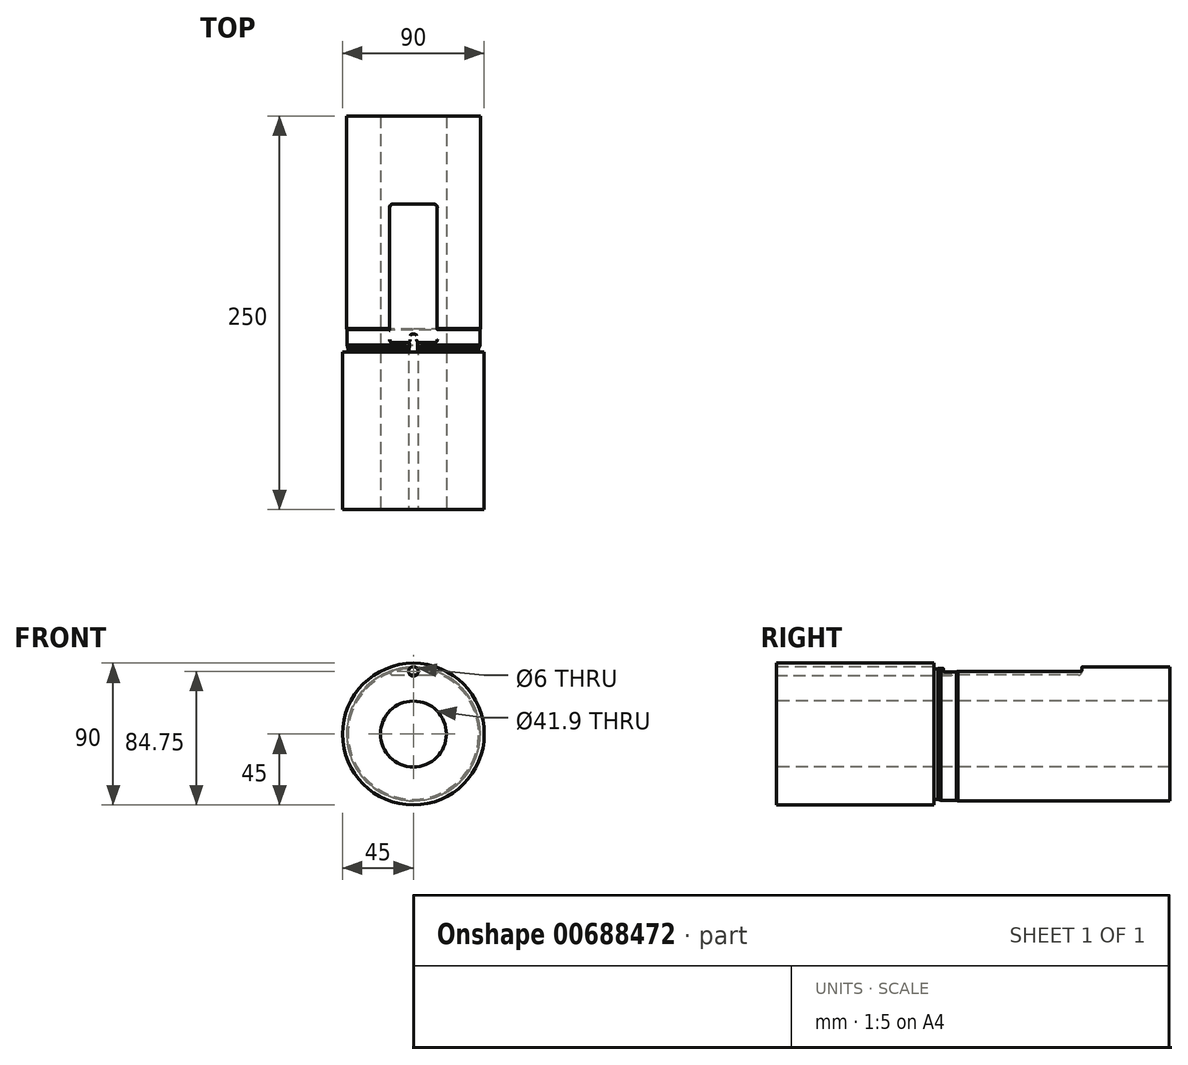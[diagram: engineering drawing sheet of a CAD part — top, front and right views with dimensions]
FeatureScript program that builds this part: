
annotation { "Feature Type Name" : "Feature", "Feature Type Description" : "" }
export const myFeature = defineFeature(function(context is Context, id is Id, definition is map)
    precondition{}
    {
        {
            var Q0;
            Q0=qCreatedBy(makeId("Right.planeOp"),FACE);
            var sketch = newSketch(context, id + "F0", { "sketchPlane" : qUnion([Q0])});
            skLineSegment(sketch, "E0", {"start": v(-100, 20.95) * mm, "end": v(-100, 45) * mm});
            skLineSegment(sketch, "E1", {"start": v(-100, 45) * mm, "end": v(0, 45) * mm});
            skLineSegment(sketch, "E2", {"start": v(0, 45) * mm, "end": v(0, 42.8) * mm});
            skArc(sketch, "E3", {"start": v(0, 42.8) * mm, "mid": v(0.38, 41.88) * mm, "end": v(1.3, 41.5) * mm});
            skLineSegment(sketch, "E4", {"start": v(4.63, 42.27) * mm, "end": v(14.4, 42.27) * mm});
            skLineSegment(sketch, "E5", {"start": v(14.4, 42.27) * mm, "end": v(15.2, 42.5) * mm});
            skLineSegment(sketch, "E6", {"start": v(15.2, 42.5) * mm, "end": v(150, 42.5) * mm});
            skLineSegment(sketch, "E7", {"start": v(150, 42.49) * mm, "end": v(150, 20.95) * mm});
            skLineSegment(sketch, "E8", {"start": v(-123.16, 0) * mm, "end": v(120.4, 0) * mm, "construction": true});
            skLineSegment(sketch, "E9", {"start": v(1.3, 41.5) * mm, "end": v(2.5, 41.5) * mm});
            skLineSegment(sketch, "E10", {"start": v(2.5, 41.5) * mm, "end": v(4.63, 42.27) * mm});
            skLineSegment(sketch, "E11", {"start": v(-100, 20.95) * mm, "end": v(150, 20.95) * mm});
            skSolve(sketch);
        }
        {
            var Q0;
            Q0=makeQuery(id+"F0.imprint","IMPRINT",FACE,{"disambiguationData":[TD([[makeQuery(id+"F0.imprint","IMPRINT",EDGE,{"derivedFrom":sQuery(id+"F0.wireOp",EDGE,"E0")}),-1.0]])]});
            var Q1;
            Q1=sQuery(id+"F0.wireOp",EDGE,"E8");
            revolve(context, id + "F1", {"entities" : qUnion([Q0]), "axis" : qUnion([Q1]), "revolveType" : RevolveType.FULL});
        }
        {
            var Q0;
            Q0=makeQuery(id+"F1.opRevolve","SWEPT_FACE",FACE,{"disambiguationData":[OSD([sQuery(id+"F0.wireOp",EDGE,"E0")])]});
            var sketch = newSketch(context, id + "F2", { "sketchPlane" : qUnion([Q0])});
            skCircle(sketch, "E12", {"center": v(0, 39.75) * mm, "radius": 3 * mm});
            skSolve(sketch);
        }
        {
            var Q0;
            Q0=qSketchRegion(id+"F2",true);
            extrude(context, id + "F3", {"entities" : qUnion([Q0]), "operationType" : NewBodyOperationType.REMOVE, "oppositeDirection" : true, "depth" : 111.5 * mm, "offsetDistance" : 25 * mm});
        }
        {
            var Q0;
            Q0=qCreatedBy(makeId("Right.planeOp"),FACE);
            var sketch = newSketch(context, id + "F4", { "sketchPlane" : qUnion([Q0])});
            skLineSegment(sketch, "E13", {"start": v(94, 42.5) * mm, "end": v(94, 37.5) * mm});
            skLineSegment(sketch, "E14", {"start": v(94, 37.5) * mm, "end": v(6, 37.5) * mm});
            skLineSegment(sketch, "E15", {"start": v(6, 37.5) * mm, "end": v(6, 42.5) * mm});
            skLineSegment(sketch, "E16", {"start": v(6, 42.5) * mm, "end": v(94, 42.5) * mm});
            skSolve(sketch);
        }
        {
            var Q0;
            Q0=qSketchRegion(id+"F4",true);
            extrude(context, id + "F5", {"entities" : qUnion([Q0]), "operationType" : NewBodyOperationType.REMOVE, "endBound" : BoundingType.SYMMETRIC, "oppositeDirection" : true, "depth" : 30 * mm, "offsetDistance" : 25 * mm});
        }
        {
            var Q0;
            Q0=qCreatedBy(makeId("Right.planeOp"),FACE);
            var sketch = newSketch(context, id + "F6", { "sketchPlane" : qUnion([Q0])});
            skLineSegment(sketch, "E17.bottom", {"start": v(2, 44.7) * mm, "end": v(8, 44.7) * mm});
            skLineSegment(sketch, "E17.top", {"start": v(2, 41.7) * mm, "end": v(8, 41.7) * mm});
            skLineSegment(sketch, "E17.left", {"start": v(2, 44.7) * mm, "end": v(2, 41.7) * mm});
            skLineSegment(sketch, "E17.right", {"start": v(8, 44.7) * mm, "end": v(8, 41.7) * mm});
            skSolve(sketch);
        }
        {
            var Q0;
            Q0=qSketchRegion(id+"F6",true);
            extrude(context, id + "F7", {"entities" : qUnion([Q0]), "operationType" : NewBodyOperationType.REMOVE, "endBound" : BoundingType.SYMMETRIC, "oppositeDirection" : true, "depth" : 30 * mm, "offsetDistance" : 25 * mm});
        }
        {
            var Q0;
            Q0=makeQuery(id+"F5.boolean.opBoolean","COPY",EDGE,{"derivedFrom":makeQuery(id+"F5.opExtrude","CAP_EDGE",EDGE,{"disambiguationData":[OSD([sQuery(id+"F4.wireOp",EDGE,"E15")])],"isStart":false})});
            var Q1;
            Q1=makeQuery(id+"F5.boolean.opBoolean","COPY",EDGE,{"derivedFrom":makeQuery(id+"F5.opExtrude","CAP_EDGE",EDGE,{"disambiguationData":[OSD([sQuery(id+"F4.wireOp",EDGE,"E15")])],"isStart":true})});
            var Q2;
            Q2=makeQuery(id+"F5.boolean.opBoolean","COPY",EDGE,{"derivedFrom":makeQuery(id+"F5.opExtrude","CAP_EDGE",EDGE,{"disambiguationData":[OSD([sQuery(id+"F4.wireOp",EDGE,"E13")])],"isStart":true})});
            var Q3;
            Q3=makeQuery(id+"F5.boolean.opBoolean","COPY",EDGE,{"derivedFrom":makeQuery(id+"F5.opExtrude","CAP_EDGE",EDGE,{"disambiguationData":[OSD([sQuery(id+"F4.wireOp",EDGE,"E13")])],"isStart":false})});
            var Q4;
            Q4=makeQuery(id+"F5.boolean.opBoolean","COPY",EDGE,{"derivedFrom":makeQuery(id+"F5.opExtrude","SWEPT_EDGE",EDGE,{"disambiguationData":[OSD([sQuery(id+"F4.wireOp",EDGE,"E13"),sQuery(id+"F4.wireOp",EDGE,"E14")])]})});
            var Q5;
            Q5=makeQuery(id+"F5.boolean.opBoolean","COPY",EDGE,{"derivedFrom":makeQuery(id+"F5.opExtrude","CAP_EDGE",EDGE,{"disambiguationData":[OSD([sQuery(id+"F4.wireOp",EDGE,"E14")])],"isStart":false})});
            var Q6;
            Q6=makeQuery(id+"F5.boolean.opBoolean","COPY",EDGE,{"derivedFrom":makeQuery(id+"F5.opExtrude","CAP_EDGE",EDGE,{"disambiguationData":[OSD([sQuery(id+"F4.wireOp",EDGE,"E14")])],"isStart":true})});
            var Q7;
            {var subQ0=sQuery(id+"F4.wireOp",EDGE,"E15");var subQ1=sQuery(id+"F4.wireOp",EDGE,"E14");Q7=makeQuery(id+"F5.boolean.opBoolean","COPY",EDGE,{"disambiguationData":[TD([makeQuery(id+"F5.opExtrude","CAP_FACE",FACE,{"disambiguationData":[OSD([sQuery(id+"F4.wireOp",EDGE,"E13"),subQ1,subQ0,sQuery(id+"F4.wireOp",EDGE,"E16")])],"isStart":true})])],"derivedFrom":makeQuery(id+"F5.opExtrude","SWEPT_EDGE",EDGE,{"disambiguationData":[OSD([subQ1,subQ0])]})});}
            var Q8;
            {var subQ0=sQuery(id+"F4.wireOp",EDGE,"E15");var subQ1=sQuery(id+"F4.wireOp",EDGE,"E14");Q8=makeQuery(id+"F5.boolean.opBoolean","COPY",EDGE,{"disambiguationData":[TD([makeQuery(id+"F5.opExtrude","CAP_FACE",FACE,{"disambiguationData":[OSD([sQuery(id+"F4.wireOp",EDGE,"E13"),subQ1,subQ0,sQuery(id+"F4.wireOp",EDGE,"E16")])],"isStart":false})])],"derivedFrom":makeQuery(id+"F5.opExtrude","SWEPT_EDGE",EDGE,{"disambiguationData":[OSD([subQ1,subQ0])]})});}
            fillet(context, id + "F8", {"entities" : qUnion([Q0, Q1, Q2, Q3, Q4, Q5, Q6, Q7, Q8]), "radius" : 2 * mm, "tangentPropagation" : true, "allowEdgeOverflow" : false});
        }
        {
            var Q0;
            Q0=makeQuery(id+"F3.boolean.opBoolean","COPY",EDGE,{"derivedFrom":makeQuery(id+"F3.opExtrude","CAP_EDGE",EDGE,{"disambiguationData":[OSD([sQuery(id+"F2.wireOp",EDGE,"E12")])],"isStart":false})});
            fillet(context, id + "F9", {"entities" : qUnion([Q0]), "radius" : 1 * mm, "tangentPropagation" : true, "allowEdgeOverflow" : false});
        }
        {
            var Q0;
            Q0=makeQuery(id+"F5.boolean.opBoolean","INTERSECT",EDGE,{"disambiguationData":[OD(1.0)],"derivedFrom":[makeQuery(id+"F3.boolean.opBoolean","COPY",FACE,{"derivedFrom":makeQuery(id+"F3.opExtrude","SWEPT_FACE",FACE,{"disambiguationData":[OSD([sQuery(id+"F2.wireOp",EDGE,"E12")])]})}),makeQuery(id+"F5.opExtrude","SWEPT_FACE",FACE,{"disambiguationData":[OSD([sQuery(id+"F4.wireOp",EDGE,"E15")])]})]});
            fillet(context, id + "F10", {"entities" : qUnion([Q0]), "radius" : 0.15 * mm, "tangentPropagation" : true, "allowEdgeOverflow" : false});
        }
        {
            var Q0;
            Q0=makeQuery(id+"F3.boolean.opBoolean","INTERSECT",EDGE,{"disambiguationData":[OD(1.0)],"derivedFrom":[makeQuery(id+"F1.opRevolve","SWEPT_FACE",FACE,{"disambiguationData":[OSD([sQuery(id+"F0.wireOp",EDGE,"E3")])]}),makeQuery(id+"F3.opExtrude","SWEPT_FACE",FACE,{"disambiguationData":[OSD([sQuery(id+"F2.wireOp",EDGE,"E12")])]})]});
            var Q1;
            Q1=makeQuery(id+"F3.boolean.opBoolean","INTERSECT",EDGE,{"derivedFrom":[makeQuery(id+"F1.opRevolve","SWEPT_FACE",FACE,{"disambiguationData":[OSD([sQuery(id+"F0.wireOp",EDGE,"E2")])]}),makeQuery(id+"F3.opExtrude","SWEPT_FACE",FACE,{"disambiguationData":[OSD([sQuery(id+"F2.wireOp",EDGE,"E12")])]})]});
            var Q2;
            Q2=makeQuery(id+"F3.boolean.opBoolean","INTERSECT",EDGE,{"disambiguationData":[OD(0.0)],"derivedFrom":[makeQuery(id+"F1.opRevolve","SWEPT_FACE",FACE,{"disambiguationData":[OSD([sQuery(id+"F0.wireOp",EDGE,"E3")])]}),makeQuery(id+"F3.opExtrude","SWEPT_FACE",FACE,{"disambiguationData":[OSD([sQuery(id+"F2.wireOp",EDGE,"E12")])]})]});
            var Q3;
            Q3=makeQuery(id+"F3.boolean.opBoolean","INTERSECT",EDGE,{"disambiguationData":[OD(0.0)],"derivedFrom":[makeQuery(id+"F1.opRevolve","SWEPT_FACE",FACE,{"disambiguationData":[OSD([sQuery(id+"F0.wireOp",EDGE,"E9")])]}),makeQuery(id+"F3.opExtrude","SWEPT_FACE",FACE,{"disambiguationData":[OSD([sQuery(id+"F2.wireOp",EDGE,"E12")])]})]});
            var Q4;
            Q4=makeQuery(id+"F3.boolean.opBoolean","INTERSECT",EDGE,{"disambiguationData":[OD(0.0)],"derivedFrom":[makeQuery(id+"F1.opRevolve","SWEPT_FACE",FACE,{"disambiguationData":[OSD([sQuery(id+"F0.wireOp",EDGE,"E10")])]}),makeQuery(id+"F3.opExtrude","SWEPT_FACE",FACE,{"disambiguationData":[OSD([sQuery(id+"F2.wireOp",EDGE,"E12")])]})]});
            var Q5;
            Q5=makeQuery(id+"F7.boolean.opBoolean","INTERSECT",EDGE,{"disambiguationData":[OD(0.0)],"derivedFrom":[makeQuery(id+"F3.boolean.opBoolean","COPY",FACE,{"derivedFrom":makeQuery(id+"F3.opExtrude","SWEPT_FACE",FACE,{"disambiguationData":[OSD([sQuery(id+"F2.wireOp",EDGE,"E12")])]})}),makeQuery(id+"F7.opExtrude","SWEPT_FACE",FACE,{"disambiguationData":[OSD([sQuery(id+"F6.wireOp",EDGE,"E17.top")])]})]});
            var Q6;
            Q6=makeQuery(id+"F3.boolean.opBoolean","INTERSECT",EDGE,{"disambiguationData":[OD(1.0)],"derivedFrom":[makeQuery(id+"F1.opRevolve","SWEPT_FACE",FACE,{"disambiguationData":[OSD([sQuery(id+"F0.wireOp",EDGE,"E9")])]}),makeQuery(id+"F3.opExtrude","SWEPT_FACE",FACE,{"disambiguationData":[OSD([sQuery(id+"F2.wireOp",EDGE,"E12")])]})]});
            var Q7;
            Q7=makeQuery(id+"F3.boolean.opBoolean","INTERSECT",EDGE,{"disambiguationData":[OD(1.0)],"derivedFrom":[makeQuery(id+"F1.opRevolve","SWEPT_FACE",FACE,{"disambiguationData":[OSD([sQuery(id+"F0.wireOp",EDGE,"E10")])]}),makeQuery(id+"F3.opExtrude","SWEPT_FACE",FACE,{"disambiguationData":[OSD([sQuery(id+"F2.wireOp",EDGE,"E12")])]})]});
            var Q8;
            Q8=makeQuery(id+"F7.boolean.opBoolean","INTERSECT",EDGE,{"disambiguationData":[OD(1.0)],"derivedFrom":[makeQuery(id+"F3.boolean.opBoolean","COPY",FACE,{"derivedFrom":makeQuery(id+"F3.opExtrude","SWEPT_FACE",FACE,{"disambiguationData":[OSD([sQuery(id+"F2.wireOp",EDGE,"E12")])]})}),makeQuery(id+"F7.opExtrude","SWEPT_FACE",FACE,{"disambiguationData":[OSD([sQuery(id+"F6.wireOp",EDGE,"E17.top")])]})]});
            fillet(context, id + "F11", {"entities" : qUnion([Q0, Q1, Q2, Q3, Q4, Q5, Q6, Q7, Q8]), "radius" : 0.25 * mm, "allowEdgeOverflow" : false});
        }
        {
            var Q0;
            Q0=makeQuery(id+"F5.boolean.opBoolean","INTERSECT",EDGE,{"derivedFrom":[makeQuery(id+"F1.opRevolve","SWEPT_FACE",FACE,{"disambiguationData":[OSD([sQuery(id+"F0.wireOp",EDGE,"E6")])]}),makeQuery(id+"F5.opExtrude","CAP_FACE",FACE,{"disambiguationData":[OSD([sQuery(id+"F4.wireOp",EDGE,"E13"),sQuery(id+"F4.wireOp",EDGE,"E14"),sQuery(id+"F4.wireOp",EDGE,"E15"),sQuery(id+"F4.wireOp",EDGE,"E16")])],"isStart":false})]});
            var Q1;
            Q1=makeQuery(id+"F5.boolean.opBoolean","INTERSECT",EDGE,{"derivedFrom":[makeQuery(id+"F1.opRevolve","SWEPT_FACE",FACE,{"disambiguationData":[OSD([sQuery(id+"F0.wireOp",EDGE,"E5")])]}),makeQuery(id+"F5.opExtrude","CAP_FACE",FACE,{"disambiguationData":[OSD([sQuery(id+"F4.wireOp",EDGE,"E13"),sQuery(id+"F4.wireOp",EDGE,"E14"),sQuery(id+"F4.wireOp",EDGE,"E15"),sQuery(id+"F4.wireOp",EDGE,"E16")])],"isStart":true})]});
            var Q2;
            Q2=makeQuery(id+"F5.boolean.opBoolean","INTERSECT",EDGE,{"derivedFrom":[makeQuery(id+"F1.opRevolve","SWEPT_FACE",FACE,{"disambiguationData":[OSD([sQuery(id+"F0.wireOp",EDGE,"E4")])]}),makeQuery(id+"F5.opExtrude","CAP_FACE",FACE,{"disambiguationData":[OSD([sQuery(id+"F4.wireOp",EDGE,"E13"),sQuery(id+"F4.wireOp",EDGE,"E14"),sQuery(id+"F4.wireOp",EDGE,"E15"),sQuery(id+"F4.wireOp",EDGE,"E16")])],"isStart":true})]});
            var Q3;
            {var subQ0=sQuery(id+"F4.wireOp",EDGE,"E15");var subQ1=sQuery(id+"F4.wireOp",EDGE,"E14");Q3=makeQuery(id+"F7.boolean.opBoolean","INTERSECT",EDGE,{"derivedFrom":[makeQuery(id+"F5.boolean.opBoolean","COPY",FACE,{"disambiguationData":[TD([makeQuery(id+"F5.opExtrude","CAP_FACE",FACE,{"disambiguationData":[OSD([sQuery(id+"F4.wireOp",EDGE,"E13"),subQ1,subQ0,sQuery(id+"F4.wireOp",EDGE,"E16")])],"isStart":true})])],"derivedFrom":makeQuery(id+"F5.opExtrude","SWEPT_FACE",FACE,{"disambiguationData":[OSD([subQ0])]})}),makeQuery(id+"F7.opExtrude","SWEPT_FACE",FACE,{"disambiguationData":[OSD([sQuery(id+"F6.wireOp",EDGE,"E17.top")])]})]});}
            var Q4;
            {var subQ0=makeQuery(id+"F3.boolean.opBoolean","COPY",FACE,{"derivedFrom":makeQuery(id+"F3.opExtrude","SWEPT_FACE",FACE,{"disambiguationData":[OSD([sQuery(id+"F2.wireOp",EDGE,"E12")])]})});var subQ1=sQuery(id+"F4.wireOp",EDGE,"E15");var subQ2=sQuery(id+"F4.wireOp",EDGE,"E14");Q4=makeQuery(id+"F11.opFillet","BLEND_EDGE",EDGE,{"blendedFrom":[makeQuery(id+"F7.boolean.opBoolean","INTERSECT",EDGE,{"disambiguationData":[OD(0.0)],"derivedFrom":[subQ0,makeQuery(id+"F7.opExtrude","SWEPT_FACE",FACE,{"disambiguationData":[OSD([sQuery(id+"F6.wireOp",EDGE,"E17.top")])]})]}),makeQuery(id+"F5.boolean.opBoolean","COPY",FACE,{"disambiguationData":[TD([makeQuery(id+"F5.opExtrude","CAP_FACE",FACE,{"disambiguationData":[OSD([sQuery(id+"F4.wireOp",EDGE,"E13"),subQ2,subQ1,sQuery(id+"F4.wireOp",EDGE,"E16")])],"isStart":false})])],"derivedFrom":makeQuery(id+"F5.opExtrude","SWEPT_FACE",FACE,{"disambiguationData":[OSD([subQ1])]})})],"blendedInto":[makeQuery(id+"F5.boolean.opBoolean","COPY",FACE,{"disambiguationData":[TD([makeQuery(id+"F5.opExtrude","CAP_FACE",FACE,{"disambiguationData":[OSD([sQuery(id+"F4.wireOp",EDGE,"E13"),subQ2,subQ1,sQuery(id+"F4.wireOp",EDGE,"E16")])],"isStart":false})])],"derivedFrom":makeQuery(id+"F5.opExtrude","SWEPT_FACE",FACE,{"disambiguationData":[OSD([subQ1])]})})]});}
            var Q5;
            Q5=makeQuery(id+"F5.boolean.opBoolean","INTERSECT",EDGE,{"disambiguationData":[OD(1.0)],"derivedFrom":[makeQuery(id+"F1.opRevolve","SWEPT_FACE",FACE,{"disambiguationData":[OSD([sQuery(id+"F0.wireOp",EDGE,"E4")])]}),makeQuery(id+"F5.opExtrude","SWEPT_FACE",FACE,{"disambiguationData":[OSD([sQuery(id+"F4.wireOp",EDGE,"E15")])]})]});
            fillet(context, id + "F12", {"entities" : qUnion([Q0, Q1, Q2, Q3, Q4, Q5]), "radius" : 0.15 * mm, "tangentPropagation" : true, "allowEdgeOverflow" : false});
        }
    });
